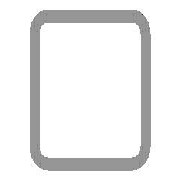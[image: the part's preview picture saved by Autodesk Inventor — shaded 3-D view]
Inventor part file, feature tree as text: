
AUTODESK INVENTOR PART (.ipt)
format: ipt  version: 2025 (Build 290162010, 162A)  size: 260,608 bytes
history: native  units: mm (DEFAULTED — no unit token found)
features: sketch x8, extrude x4, other x3, hole x3, fillet x2, plane x1, projected_geometry x1
ambient origin geometry x8: Origin, YZ Plane, XZ Plane, XY Plane, X Axis, Y Axis, Z Axis, Center Point
bodies: Solid1 (feature_tree)
feature tree (22):
  other  "Driven Length"
  other  "Startebene"
  other  "Endebene"
  extrude  "Körper"  TaperAngle=0.0deg  [1 undecoded]
  extrude  "Extrusion2"  Depth=20.0mm
  hole  "Bohrung5"  [1 undecoded]
  hole  "Bohrung7"  [1 undecoded]
  sketch  "Skizze13"  dims[d17=90.0deg d18=200.0mm]
  extrude  "Extrusion3"  Depth=10.0mm
  extrude  "Extrusion4"  Depth=200.0mm
  hole  "Bohrung6"  [1 undecoded]
  fillet  "Rundung3"  [1 undecoded]
  fillet  "Rundung4"  Radius=16.0mm
  sketch  "Sketch3"  dims[d3=200.0mm d4=0.0mm]
  plane  "Work Plane3"
  sketch  "Skizze9"  dims[d7=3.0mm d10=20.0mm]
  sketch  "Skizze10"  dims[d11=20.0mm d12=2.0mm]
  sketch  "Skizze11"  dims[d13=-0.0mm d14=200.0mm]
  sketch  "Skizze12"  dims[d15=10.0mm d16=10.0mm]
  sketch  "Skizze14"  dims[d47=6.0mm d48=35.0mm d49=0.0mm d50=0.0mm d51=16.0mm]
  projected_geometry  "Projizierte Kontur1"
  sketch  "Skizze15"  dims[d52=2.459mm d53=50.0mm d54=4.0mm d55=2.0mm d56=90.0deg d57=7.8mm d58=20.594885mm d59=5.0mm d60=3.0mm d61=5.0mm d62=4.0mm d63=2.0mm d64=90.0deg d65=6.3mm d66=20.594885mm d67=110.0mm d68=3.2mm d69=6.0mm d70=6.3mm d71=2.0mm d72=90.0deg d73=8.0mm d74=20.594885mm d75=30.0mm d76=0.0mm d77=30.0mm d78=0.0mm d79=0.0mm d80=1.0mm d81=1.0mm]
note: 5 required parameter values undecoded (feature->parameter linkage not recoverable at this tier; creation-order binding heuristic only, values carry confidence <= 0.55)
